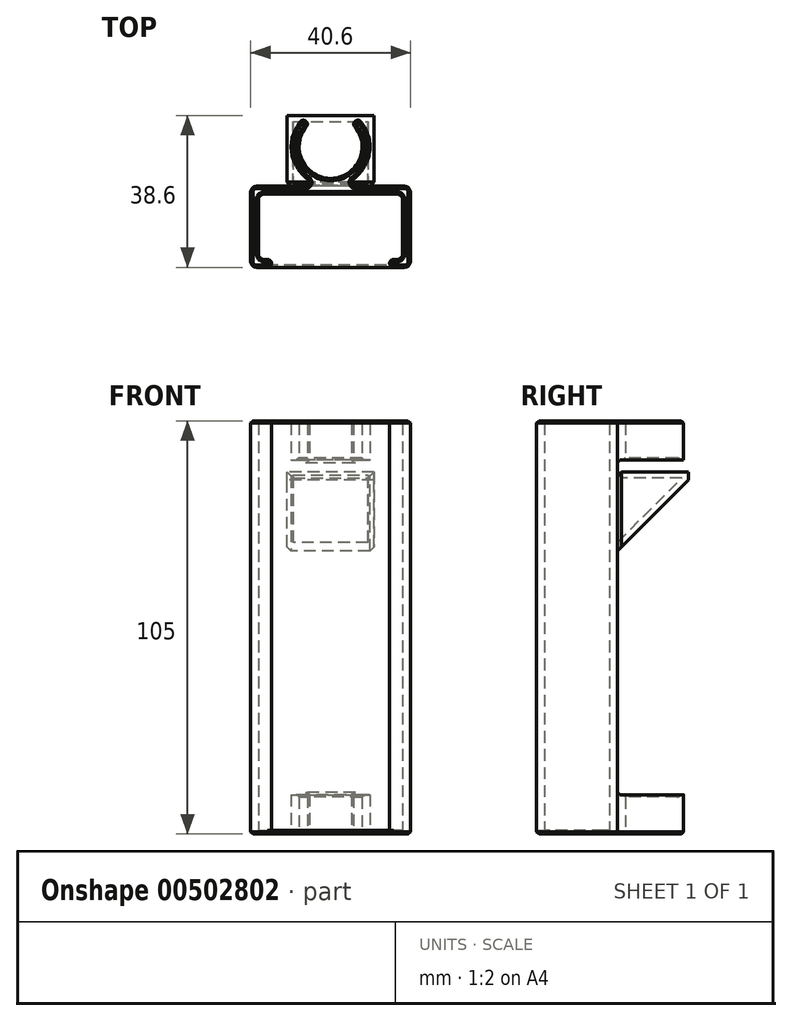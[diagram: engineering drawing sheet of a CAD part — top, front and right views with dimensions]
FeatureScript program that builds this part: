
annotation { "Feature Type Name" : "Feature", "Feature Type Description" : "" }
export const myFeature = defineFeature(function(context is Context, id is Id, definition is map)
    precondition{}
    {
        {
            var Q0;
            Q0=qCreatedBy(makeId("Top.planeOp"),FACE);
            var sketch = newSketch(context, id + "F0", { "sketchPlane" : qUnion([Q0])});
            skArc(sketch, "E0", {"start": v(-6.13, 5.14) * mm, "mid": v(0, -8) * mm, "end": v(6.13, 5.14) * mm});
            skArc(sketch, "E1", {"start": v(-7.66, 6.43) * mm, "mid": v(-9.92, -1.3) * mm, "end": v(-5.75, -8.18) * mm});
            skLineSegment(sketch, "E2", {"start": v(-7.66, 6.43) * mm, "end": v(0, 0) * mm, "construction": true});
            skLineSegment(sketch, "E3", {"start": v(0, 0) * mm, "end": v(7.66, 6.43) * mm, "construction": true});
            skArc(sketch, "E4", {"start": v(-6.13, 5.14) * mm, "mid": v(-6.25, 6.55) * mm, "end": v(-7.66, 6.43) * mm});
            skArc(sketch, "E5.MirrorCS", {"start": v(6.13, 5.14) * mm, "mid": v(6.25, 6.55) * mm, "end": v(7.66, 6.43) * mm});
            skLineSegment(sketch, "E6", {"start": v(6.32, -10) * mm, "end": v(18.8, -10) * mm});
            skLineSegment(sketch, "E7", {"start": v(20.3, -11.5) * mm, "end": v(20.3, -29.1) * mm});
            skLineSegment(sketch, "E8", {"start": v(18.8, -30.6) * mm, "end": v(16, -30.6) * mm});
            skLineSegment(sketch, "E9", {"start": v(16, -30.6) * mm, "end": v(16, -28.6) * mm, "construction": true});
            skLineSegment(sketch, "E10.0", {"start": v(16.8, -28.6) * mm, "end": v(16, -28.6) * mm});
            skLineSegment(sketch, "E10.1", {"start": v(18.3, -13.5) * mm, "end": v(18.3, -27.1) * mm});
            skLineSegment(sketch, "E10.2", {"start": v(0, -12) * mm, "end": v(16.8, -12) * mm});
            skArc(sketch, "E11", {"start": v(16, -28.6) * mm, "mid": v(15, -29.6) * mm, "end": v(16, -30.6) * mm});
            skArc(sketch, "E12.MirrorCS", {"start": v(-16, -28.6) * mm, "mid": v(-15, -29.6) * mm, "end": v(-16, -30.6) * mm});
            skLineSegment(sketch, "E13.MirrorCS", {"start": v(-16, -30.6) * mm, "end": v(-16, -28.6) * mm, "construction": true});
            skLineSegment(sketch, "E14.MirrorCS", {"start": v(0, -12) * mm, "end": v(-16.8, -12) * mm});
            skLineSegment(sketch, "E15.MirrorCS", {"start": v(-18.3, -13.5) * mm, "end": v(-18.3, -27.1) * mm});
            skLineSegment(sketch, "E16.MirrorCS", {"start": v(-16.8, -28.6) * mm, "end": v(-16, -28.6) * mm});
            skLineSegment(sketch, "E17.MirrorCS", {"start": v(-20.3, -11.5) * mm, "end": v(-20.3, -29.1) * mm});
            skLineSegment(sketch, "E18.MirrorCS", {"start": v(-18.8, -30.6) * mm, "end": v(-16, -30.6) * mm});
            skLineSegment(sketch, "E19.MirrorCS", {"start": v(-6.32, -10) * mm, "end": v(-18.8, -10) * mm});
            skArc(sketch, "E20.trimOffspring", {"start": v(5.75, -8.18) * mm, "mid": v(9.92, -1.3) * mm, "end": v(7.66, 6.43) * mm});
            skPoint(sketch, "E21.visualSharp", {"position": v(20.3, -10) * mm});
            skArc(sketch, "E21.filletArc", {"start": v(20.3, -11.5) * mm, "mid": v(19.86, -10.44) * mm, "end": v(18.8, -10) * mm});
            skPoint(sketch, "E22.visualSharp", {"position": v(18.3, -28.6) * mm});
            skArc(sketch, "E22.filletArc", {"start": v(16.8, -28.6) * mm, "mid": v(17.86, -28.16) * mm, "end": v(18.3, -27.1) * mm});
            skPoint(sketch, "E23.visualSharp", {"position": v(20.3, -30.6) * mm});
            skArc(sketch, "E23.filletArc", {"start": v(18.8, -30.6) * mm, "mid": v(19.86, -30.16) * mm, "end": v(20.3, -29.1) * mm});
            skPoint(sketch, "E24.visualSharp", {"position": v(-18.3, -28.6) * mm});
            skArc(sketch, "E24.filletArc", {"start": v(-18.3, -27.1) * mm, "mid": v(-17.86, -28.16) * mm, "end": v(-16.8, -28.6) * mm});
            skPoint(sketch, "E25.visualSharp", {"position": v(-20.3, -30.6) * mm});
            skArc(sketch, "E25.filletArc", {"start": v(-20.3, -29.1) * mm, "mid": v(-19.86, -30.16) * mm, "end": v(-18.8, -30.6) * mm});
            skPoint(sketch, "E26.visualSharp", {"position": v(-18.3, -12) * mm});
            skArc(sketch, "E26.filletArc", {"start": v(-16.8, -12) * mm, "mid": v(-17.86, -12.44) * mm, "end": v(-18.3, -13.5) * mm});
            skPoint(sketch, "E27.visualSharp", {"position": v(-20.3, -10) * mm});
            skArc(sketch, "E27.filletArc", {"start": v(-18.8, -10) * mm, "mid": v(-19.86, -10.44) * mm, "end": v(-20.3, -11.5) * mm});
            skPoint(sketch, "E28.visualSharp", {"position": v(18.3, -12) * mm});
            skArc(sketch, "E28.filletArc", {"start": v(18.3, -13.5) * mm, "mid": v(17.86, -12.44) * mm, "end": v(16.8, -12) * mm});
            skPoint(sketch, "E29.visualSharp", {"position": v(0, -10) * mm});
            skArc(sketch, "E29.filletArc", {"start": v(5.75, -8.18) * mm, "mid": v(5.37, -9.3) * mm, "end": v(6.32, -10) * mm});
            skArc(sketch, "E30.filletArc", {"start": v(-6.32, -10) * mm, "mid": v(-5.37, -9.3) * mm, "end": v(-5.75, -8.18) * mm});
            skLineSegment(sketch, "E31", {"start": v(-16, -30.6) * mm, "end": v(16, -30.6) * mm});
            skSolve(sketch);
        }
        {
            var Q0;
            Q0=makeQuery(id+"F0.imprint","IMPRINT",FACE,{"disambiguationData":[TD([[makeQuery(id+"F0.imprint","IMPRINT",EDGE,{"derivedFrom":sQuery(id+"F0.wireOp",EDGE,"E0")}),-1.0]])]});
            extrude(context, id + "F1", {"entities" : qUnion([Q0]), "depth" : 105 * mm, "offsetDistance" : 25 * mm});
        }
        {
            var Q0;
            Q0=makeQuery(id+"F0.imprint","IMPRINT",FACE,{"disambiguationData":[TD([[makeQuery(id+"F0.imprint","IMPRINT",EDGE,{"derivedFrom":sQuery(id+"F0.wireOp",EDGE,"E10.0")}),-1.0]])]});
            extrude(context, id + "F2", {"entities" : qUnion([Q0]), "operationType" : NewBodyOperationType.ADD, "depth" : 1 * mm, "offsetDistance" : 25 * mm});
        }
        {
            var Q0;
            Q0=makeQuery(id+"F1.opExtrude","SWEPT_FACE",FACE,{"disambiguationData":[OSD([sQuery(id+"F0.wireOp",EDGE,"E17.MirrorCS")])]});
            var sketch = newSketch(context, id + "F3", { "sketchPlane" : qUnion([Q0])});
            skLineSegment(sketch, "E32.bottom", {"start": v(-20, 95) * mm, "end": v(10, 95) * mm});
            skLineSegment(sketch, "E32.top", {"start": v(-20, 10) * mm, "end": v(10, 10) * mm});
            skLineSegment(sketch, "E32.left", {"start": v(-20, 95) * mm, "end": v(-20, 10) * mm});
            skLineSegment(sketch, "E32.right", {"start": v(10, 95) * mm, "end": v(10, 10) * mm});
            skSolve(sketch);
        }
        {
            var Q0;
            Q0 = qSketchRegion(id + "F3", true);
            extrude(context, id + "F4", {"entities" : qUnion([Q0]), "operationType" : NewBodyOperationType.REMOVE, "endBound" : BoundingType.THROUGH_ALL, "oppositeDirection" : true, "depth" : 25 * mm, "offsetDistance" : 25 * mm});
        }
        {
            var Q0;
            Q0=makeQuery(id+"F1.opExtrude","CAP_FACE",FACE,{"disambiguationData":[OSD([sQuery(id+"F0.wireOp",EDGE,"E0"),sQuery(id+"F0.wireOp",EDGE,"E1"),sQuery(id+"F0.wireOp",EDGE,"E4"),sQuery(id+"F0.wireOp",EDGE,"E5.MirrorCS"),sQuery(id+"F0.wireOp",EDGE,"E6"),sQuery(id+"F0.wireOp",EDGE,"E7"),sQuery(id+"F0.wireOp",EDGE,"E8"),sQuery(id+"F0.wireOp",EDGE,"E10.0"),sQuery(id+"F0.wireOp",EDGE,"E10.1"),sQuery(id+"F0.wireOp",EDGE,"E10.2"),sQuery(id+"F0.wireOp",EDGE,"E11"),sQuery(id+"F0.wireOp",EDGE,"E12.MirrorCS"),sQuery(id+"F0.wireOp",EDGE,"E14.MirrorCS"),sQuery(id+"F0.wireOp",EDGE,"E15.MirrorCS"),sQuery(id+"F0.wireOp",EDGE,"E16.MirrorCS"),sQuery(id+"F0.wireOp",EDGE,"E17.MirrorCS"),sQuery(id+"F0.wireOp",EDGE,"E18.MirrorCS"),sQuery(id+"F0.wireOp",EDGE,"E19.MirrorCS"),sQuery(id+"F0.wireOp",EDGE,"E20.trimOffspring"),sQuery(id+"F0.wireOp",EDGE,"E21.filletArc"),sQuery(id+"F0.wireOp",EDGE,"E22.filletArc"),sQuery(id+"F0.wireOp",EDGE,"E23.filletArc"),sQuery(id+"F0.wireOp",EDGE,"E24.filletArc"),sQuery(id+"F0.wireOp",EDGE,"E25.filletArc"),sQuery(id+"F0.wireOp",EDGE,"E26.filletArc"),sQuery(id+"F0.wireOp",EDGE,"E27.filletArc"),sQuery(id+"F0.wireOp",EDGE,"E28.filletArc"),sQuery(id+"F0.wireOp",EDGE,"E29.filletArc"),sQuery(id+"F0.wireOp",EDGE,"E30.filletArc")])],"isStart":false});
            var Q1;
            Q1=makeQuery(id+"F4.boolean.opBoolean","INTERSECT",EDGE,{"derivedFrom":[makeQuery(id+"F1.opExtrude","SWEPT_FACE",FACE,{"disambiguationData":[OSD([sQuery(id+"F0.wireOp",EDGE,"E0")])]}),makeQuery(id+"F4.opExtrude","SWEPT_FACE",FACE,{"disambiguationData":[OSD([sQuery(id+"F3.wireOp",EDGE,"E32.top")])]})]});
            var Q2;
            Q2=makeQuery(id+"F4.boolean.opBoolean","COPY",EDGE,{"derivedFrom":makeQuery(id+"F4.opExtrude","SWEPT_EDGE",EDGE,{"disambiguationData":[OSD([sQuery(id+"F3.wireOp",EDGE,"E32.top"),sQuery(id+"F3.wireOp",EDGE,"E32.right")])]})});
            var Q3;
            Q3=makeQuery(id+"F4.boolean.opBoolean","INTERSECT",EDGE,{"derivedFrom":[makeQuery(id+"F1.opExtrude","SWEPT_FACE",FACE,{"disambiguationData":[OSD([sQuery(id+"F0.wireOp",EDGE,"E0")])]}),makeQuery(id+"F4.opExtrude","SWEPT_FACE",FACE,{"disambiguationData":[OSD([sQuery(id+"F3.wireOp",EDGE,"E32.bottom")])]})]});
            var Q4;
            Q4=makeQuery(id+"F4.boolean.opBoolean","COPY",EDGE,{"derivedFrom":makeQuery(id+"F4.opExtrude","SWEPT_EDGE",EDGE,{"disambiguationData":[OSD([sQuery(id+"F3.wireOp",EDGE,"E32.bottom"),sQuery(id+"F3.wireOp",EDGE,"E32.right")])]})});
            var Q5;
            {var subQ0=sQuery(id+"F0.wireOp",EDGE,"E28.filletArc");var subQ1=sQuery(id+"F0.wireOp",EDGE,"E26.filletArc");var subQ2=sQuery(id+"F0.wireOp",EDGE,"E24.filletArc");var subQ3=sQuery(id+"F0.wireOp",EDGE,"E22.filletArc");var subQ4=sQuery(id+"F0.wireOp",EDGE,"E16.MirrorCS");var subQ5=sQuery(id+"F0.wireOp",EDGE,"E15.MirrorCS");var subQ6=sQuery(id+"F0.wireOp",EDGE,"E14.MirrorCS");var subQ7=sQuery(id+"F0.wireOp",EDGE,"E12.MirrorCS");var subQ8=sQuery(id+"F0.wireOp",EDGE,"E11");var subQ9=sQuery(id+"F0.wireOp",EDGE,"E10.2");var subQ10=sQuery(id+"F0.wireOp",EDGE,"E10.1");var subQ11=sQuery(id+"F0.wireOp",EDGE,"E10.0");Q5=makeQuery(id+"F2.boolean.opBoolean","MERGE",FACE,{"derivedFrom":[makeQuery(id+"F1.opExtrude","CAP_FACE",FACE,{"disambiguationData":[OSD([sQuery(id+"F0.wireOp",EDGE,"E0"),sQuery(id+"F0.wireOp",EDGE,"E1"),sQuery(id+"F0.wireOp",EDGE,"E4"),sQuery(id+"F0.wireOp",EDGE,"E5.MirrorCS"),sQuery(id+"F0.wireOp",EDGE,"E6"),sQuery(id+"F0.wireOp",EDGE,"E7"),sQuery(id+"F0.wireOp",EDGE,"E8"),subQ11,subQ10,subQ9,subQ8,subQ7,subQ6,subQ5,subQ4,sQuery(id+"F0.wireOp",EDGE,"E17.MirrorCS"),sQuery(id+"F0.wireOp",EDGE,"E18.MirrorCS"),sQuery(id+"F0.wireOp",EDGE,"E19.MirrorCS"),sQuery(id+"F0.wireOp",EDGE,"E20.trimOffspring"),sQuery(id+"F0.wireOp",EDGE,"E21.filletArc"),subQ3,sQuery(id+"F0.wireOp",EDGE,"E23.filletArc"),subQ2,sQuery(id+"F0.wireOp",EDGE,"E25.filletArc"),subQ1,sQuery(id+"F0.wireOp",EDGE,"E27.filletArc"),subQ0,sQuery(id+"F0.wireOp",EDGE,"E29.filletArc"),sQuery(id+"F0.wireOp",EDGE,"E30.filletArc")])],"isStart":true}),makeQuery(id+"F2.opExtrude","CAP_FACE",FACE,{"disambiguationData":[OSD([subQ11,subQ10,subQ9,subQ8,subQ7,subQ6,subQ5,subQ4,subQ3,subQ2,subQ1,subQ0,sQuery(id+"F0.wireOp",EDGE,"E31")])],"isStart":true})]});}
            var Q6;
            Q6=makeQuery(id+"F2.opExtrude","CAP_EDGE",EDGE,{"disambiguationData":[OSD([sQuery(id+"F0.wireOp",EDGE,"E10.2"),sQuery(id+"F0.wireOp",EDGE,"E14.MirrorCS")])],"isStart":false});
            var Q7;
            Q7=makeQuery(id+"F2.opExtrude","CAP_EDGE",EDGE,{"disambiguationData":[OSD([sQuery(id+"F0.wireOp",EDGE,"E10.1")])],"isStart":false});
            var Q8;
            Q8=makeQuery(id+"F2.opExtrude","CAP_EDGE",EDGE,{"disambiguationData":[OSD([sQuery(id+"F0.wireOp",EDGE,"E15.MirrorCS")])],"isStart":false});
            chamfer(context, id + "F5", {"entities" : qUnion([Q0, Q1, Q2, Q3, Q4, Q5, Q6, Q7, Q8]), "width" : 0.6 * mm});
        }
        {
            var Q0;
            Q0=qCreatedBy(makeId("Right.planeOp"),FACE);
            var sketch = newSketch(context, id + "F6", { "sketchPlane" : qUnion([Q0])});
            skLineSegment(sketch, "E33", {"start": v(8, 90) * mm, "end": v(8, 92) * mm});
            skLineSegment(sketch, "E34", {"start": v(8, 92) * mm, "end": v(-9, 92) * mm});
            skLineSegment(sketch, "E35", {"start": v(-9, 92) * mm, "end": v(-10, 91) * mm});
            skLineSegment(sketch, "E36", {"start": v(-10, 91) * mm, "end": v(-10, 72) * mm});
            skLineSegment(sketch, "E37", {"start": v(-10, 72) * mm, "end": v(8, 90) * mm});
            skSolve(sketch);
        }
        {
            var Q0;
            Q0 = qSketchRegion(id + "F6", true);
            extrude(context, id + "F7", {"entities" : qUnion([Q0]), "depth" : 22 * mm, "offsetDistance" : 25 * mm, "symmetric" : true});
        }
        {
            var Q0;
            Q0=makeQuery(id+"F7.opExtrude","SWEPT_FACE",FACE,{"disambiguationData":[OSD([sQuery(id+"F6.wireOp",EDGE,"E36")])]});
            var Q1;
            Q1=makeQuery(id+"F7.opExtrude","SWEPT_FACE",FACE,{"disambiguationData":[OSD([sQuery(id+"F6.wireOp",EDGE,"E35")])]});
            shell(context, id + "F8", {"entities" : qUnion([Q0, Q1]), "thickness" : 1.5 * mm});
        }
        {
            var Q0;
            Q0=makeQuery(id+"F7.opExtrude","CAP_EDGE",EDGE,{"disambiguationData":[OSD([sQuery(id+"F6.wireOp",EDGE,"E36")])],"isStart":true});
            var Q1;
            Q1=makeQuery(id+"F7.opExtrude","CAP_EDGE",EDGE,{"disambiguationData":[OSD([sQuery(id+"F6.wireOp",EDGE,"E36")])],"isStart":false});
            var Q2;
            Q2=makeQuery(id+"F8.opShell","TWEAK_EDGE",EDGE,{"derivedFrom":[makeQuery(id+"F7.opExtrude","SWEPT_FACE",FACE,{"disambiguationData":[OSD([sQuery(id+"F6.wireOp",EDGE,"E34")])]}),makeQuery(id+"F7.opExtrude","SWEPT_FACE",FACE,{"disambiguationData":[OSD([sQuery(id+"F6.wireOp",EDGE,"E36")])]})]});
            chamfer(context, id + "F9", {"entities" : qUnion([Q0, Q1, Q2]), "width" : 1 * mm, "tangentPropagation" : true});
        }
    });
